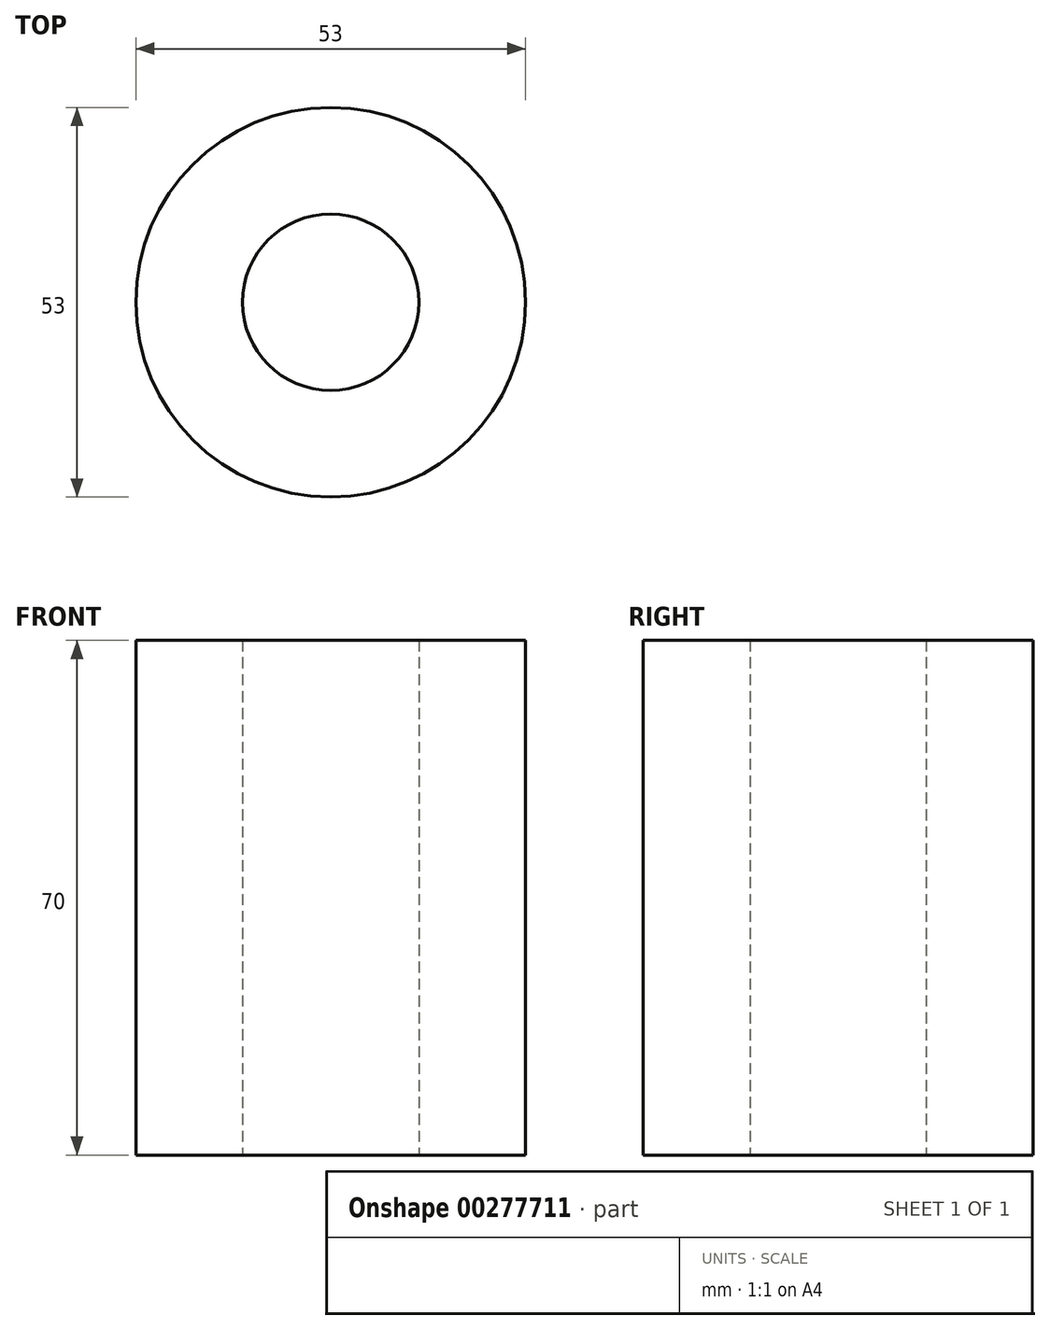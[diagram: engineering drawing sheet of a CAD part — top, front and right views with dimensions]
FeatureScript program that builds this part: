
annotation { "Feature Type Name" : "Feature", "Feature Type Description" : "" }
export const myFeature = defineFeature(function(context is Context, id is Id, definition is map)
    precondition{}
    {
        {
            var Q0;
            Q0=qCreatedBy(makeId("Top.planeOp"),FACE);
            var sketch = newSketch(context, id + "F0", { "sketchPlane" : qUnion([Q0])});
            skCircle(sketch, "E0", {"center": v(0, 0) * mm, "radius": 26.5 * mm});
            skCircle(sketch, "E1", {"center": v(0, 0) * mm, "radius": 12 * mm});
            skSolve(sketch);
        }
        {
            var Q0;
            Q0=makeQuery(id+"F0.imprint","IMPRINT",FACE,{"disambiguationData":[TD([[makeQuery(id+"F0.imprint","IMPRINT",EDGE,{"derivedFrom":sQuery(id+"F0.wireOp",EDGE,"E0")}),1.0]])]});
            extrude(context, id + "F1", {"entities" : qUnion([Q0]), "depth" : 70 * mm});
        }
    });
